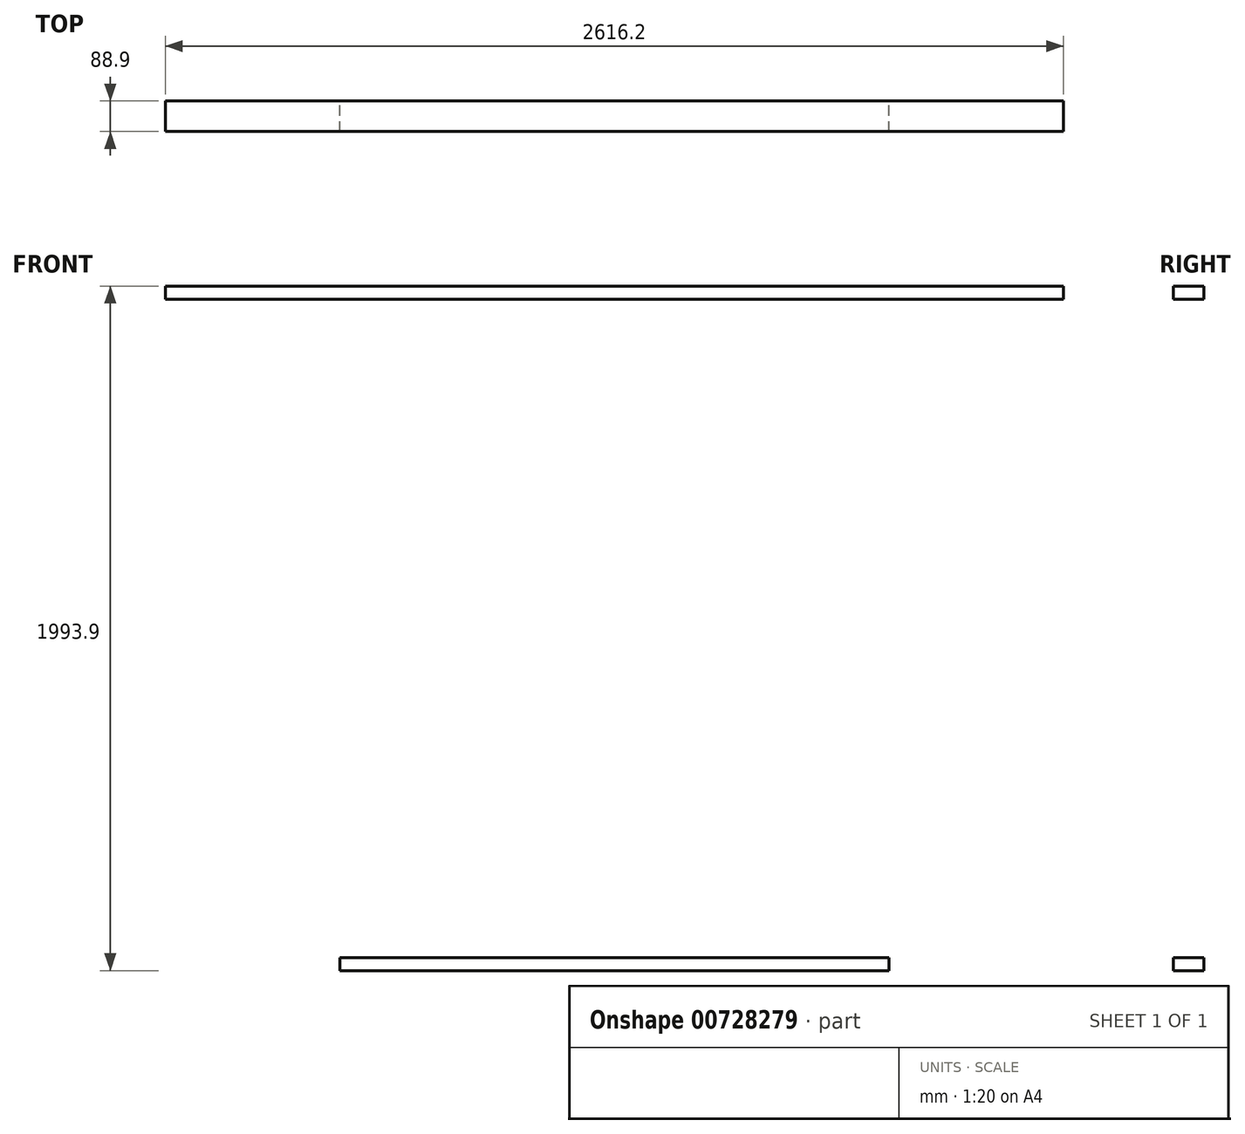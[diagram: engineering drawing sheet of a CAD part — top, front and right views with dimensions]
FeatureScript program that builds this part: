
annotation { "Feature Type Name" : "Feature", "Feature Type Description" : "" }
export const myFeature = defineFeature(function(context is Context, id is Id, definition is map)
    precondition{}
    {
        {
            var Q0;
            Q0=qCreatedBy(makeId("Front.planeOp"),FACE);
            var sketch = newSketch(context, id + "F0", { "sketchPlane" : qUnion([Q0])});
            skLineSegment(sketch, "E0.bottom", {"start": v(-1308.1, -1181.1) * mm, "end": v(1308.1, -1181.1) * mm});
            skLineSegment(sketch, "E0.top", {"start": v(-1308.1, 1181.1) * mm, "end": v(1308.1, 1181.1) * mm});
            skLineSegment(sketch, "E0.left", {"start": v(-1308.1, -1181.1) * mm, "end": v(-1308.1, 1181.1) * mm});
            skLineSegment(sketch, "E0.right", {"start": v(1308.1, -1181.1) * mm, "end": v(1308.1, 1181.1) * mm});
            skPoint(sketch, "E0.middle", {"position": v(0, 0) * mm});
            skLineSegment(sketch, "E1.0", {"start": v(-1308.1, 1143) * mm, "end": v(1308.1, 1143) * mm});
            skLineSegment(sketch, "E2.bottom", {"start": v(838.2, 1143) * mm, "end": v(800.1, 1143) * mm});
            skLineSegment(sketch, "E2.top", {"start": v(838.2, -1181.1) * mm, "end": v(800.1, -1181.1) * mm});
            skLineSegment(sketch, "E2.left", {"start": v(838.2, 1143) * mm, "end": v(838.2, -1181.1) * mm});
            skLineSegment(sketch, "E2.right", {"start": v(800.1, 1143) * mm, "end": v(800.1, -1181.1) * mm});
            skLineSegment(sketch, "E3.bottom", {"start": v(-838.2, 1143) * mm, "end": v(-800.1, 1143) * mm});
            skLineSegment(sketch, "E3.top", {"start": v(-838.2, -1181.1) * mm, "end": v(-800.1, -1181.1) * mm});
            skLineSegment(sketch, "E3.left", {"start": v(-838.2, 1143) * mm, "end": v(-838.2, -1181.1) * mm});
            skLineSegment(sketch, "E3.right", {"start": v(-800.1, 1143) * mm, "end": v(-800.1, -1181.1) * mm});
            skLineSegment(sketch, "E4.bottom", {"start": v(-800.1, -774.7) * mm, "end": v(800.1, -774.7) * mm});
            skLineSegment(sketch, "E4.top", {"start": v(-800.1, -812.8) * mm, "end": v(800.1, -812.8) * mm});
            skLineSegment(sketch, "E4.left", {"start": v(-800.1, -774.7) * mm, "end": v(-800.1, -812.8) * mm});
            skLineSegment(sketch, "E4.right", {"start": v(800.1, -774.7) * mm, "end": v(800.1, -812.8) * mm});
            skLineSegment(sketch, "E5.bottom", {"start": v(514.35, -812.8) * mm, "end": v(476.25, -812.8) * mm});
            skLineSegment(sketch, "E5.top", {"start": v(514.35, -1181.1) * mm, "end": v(476.25, -1181.1) * mm});
            skLineSegment(sketch, "E5.left", {"start": v(514.35, -812.8) * mm, "end": v(514.35, -1181.1) * mm});
            skLineSegment(sketch, "E5.right", {"start": v(476.25, -812.8) * mm, "end": v(476.25, -1181.1) * mm});
            skLineSegment(sketch, "E6.bottom", {"start": v(69.85, -812.8) * mm, "end": v(107.95, -812.8) * mm});
            skLineSegment(sketch, "E6.top", {"start": v(69.85, -1181.1) * mm, "end": v(107.95, -1181.1) * mm});
            skLineSegment(sketch, "E6.left", {"start": v(69.85, -812.8) * mm, "end": v(69.85, -1181.1) * mm});
            skLineSegment(sketch, "E6.right", {"start": v(107.95, -812.8) * mm, "end": v(107.95, -1181.1) * mm});
            skLineSegment(sketch, "E7.bottom", {"start": v(-298.45, -812.8) * mm, "end": v(-336.55, -812.8) * mm});
            skLineSegment(sketch, "E7.top", {"start": v(-298.45, -1181.1) * mm, "end": v(-336.55, -1181.1) * mm});
            skLineSegment(sketch, "E7.left", {"start": v(-298.45, -812.8) * mm, "end": v(-298.45, -1181.1) * mm});
            skLineSegment(sketch, "E7.right", {"start": v(-336.55, -812.8) * mm, "end": v(-336.55, -1181.1) * mm});
            skLineSegment(sketch, "E8.bottom", {"start": v(-1149.35, 1143) * mm, "end": v(-1111.25, 1143) * mm});
            skLineSegment(sketch, "E8.top", {"start": v(-1149.35, -1181.1) * mm, "end": v(-1111.25, -1181.1) * mm});
            skLineSegment(sketch, "E8.left", {"start": v(-1149.35, 1143) * mm, "end": v(-1149.35, -1181.1) * mm});
            skLineSegment(sketch, "E8.right", {"start": v(-1111.25, 1143) * mm, "end": v(-1111.25, -1181.1) * mm});
            skLineSegment(sketch, "E9.bottom", {"start": v(1092.2, 1143) * mm, "end": v(1054.1, 1143) * mm});
            skLineSegment(sketch, "E9.top", {"start": v(1092.2, -1181.1) * mm, "end": v(1054.1, -1181.1) * mm});
            skLineSegment(sketch, "E9.left", {"start": v(1092.2, 1143) * mm, "end": v(1092.2, -1181.1) * mm});
            skLineSegment(sketch, "E9.right", {"start": v(1054.1, 1143) * mm, "end": v(1054.1, -1181.1) * mm});
            skSolve(sketch);
        }
        {
            var Q0;
            Q0=makeQuery(id+"F0.imprint","IMPRINT",FACE,{"disambiguationData":[TD([[makeQuery(id+"F0.imprint","IMPRINT",EDGE,{"derivedFrom":sQuery(id+"F0.wireOp",EDGE,"E5.bottom")}),1.0]])]});
            var Q1;
            Q1=makeQuery(id+"F0.imprint","IMPRINT",FACE,{"disambiguationData":[TD([[makeQuery(id+"F0.imprint","IMPRINT",EDGE,{"derivedFrom":sQuery(id+"F0.wireOp",EDGE,"E6.bottom")}),-1.0]])]});
            var Q2;
            Q2=makeQuery(id+"F0.imprint","IMPRINT",FACE,{"disambiguationData":[TD([[makeQuery(id+"F0.imprint","IMPRINT",EDGE,{"derivedFrom":sQuery(id+"F0.wireOp",EDGE,"E7.bottom")}),1.0]])]});
            var Q3;
            Q3=makeQuery(id+"F0.imprint","IMPRINT",FACE,{"disambiguationData":[TD([[makeQuery(id+"F0.imprint","IMPRINT",EDGE,{"derivedFrom":sQuery(id+"F0.wireOp",EDGE,"E8.bottom")}),-1.0]])]});
            var Q4;
            Q4=makeQuery(id+"F0.imprint","IMPRINT",FACE,{"disambiguationData":[TD([[makeQuery(id+"F0.imprint","IMPRINT",EDGE,{"derivedFrom":sQuery(id+"F0.wireOp",EDGE,"E9.bottom")}),1.0]])]});
            var Q5;
            {var subQ1=sQuery(id+"F0.wireOp",EDGE,"E2.bottom");Q5=makeQuery(id+"F0.imprint","IMPRINT",FACE,{"disambiguationData":[TD([[makeQuery(id+"F0.imprint","IMPRINT",EDGE,{"derivedFrom":subQ1}),1.0]])]});}
            var Q6;
            {var subQ1=sQuery(id+"F0.wireOp",EDGE,"E3.bottom");Q6=makeQuery(id+"F0.imprint","IMPRINT",FACE,{"disambiguationData":[TD([[makeQuery(id+"F0.imprint","IMPRINT",EDGE,{"derivedFrom":subQ1}),-1.0]])]});}
            var Q7;
            {var subQ7=sQuery(id+"F0.wireOp",EDGE,"E0.top");Q7=makeQuery(id+"F0.imprint","IMPRINT",FACE,{"disambiguationData":[TD([[makeQuery(id+"F0.imprint","IMPRINT",EDGE,{"derivedFrom":subQ7}),-1.0]])]});}
            var Q8;
            Q8=makeQuery(id+"F0.imprint","IMPRINT",FACE,{"disambiguationData":[TD([[makeQuery(id+"F0.imprint","IMPRINT",EDGE,{"derivedFrom":sQuery(id+"F0.wireOp",EDGE,"E4.bottom")}),-1.0]])]});
            extrude(context, id + "F1", {"entities" : qUnion([Q0, Q1, Q2, Q3, Q4, Q5, Q6, Q7, Q8]), "depth" : 88.9 * mm, "offsetDistance" : 25.4 * mm});
        }
    });
